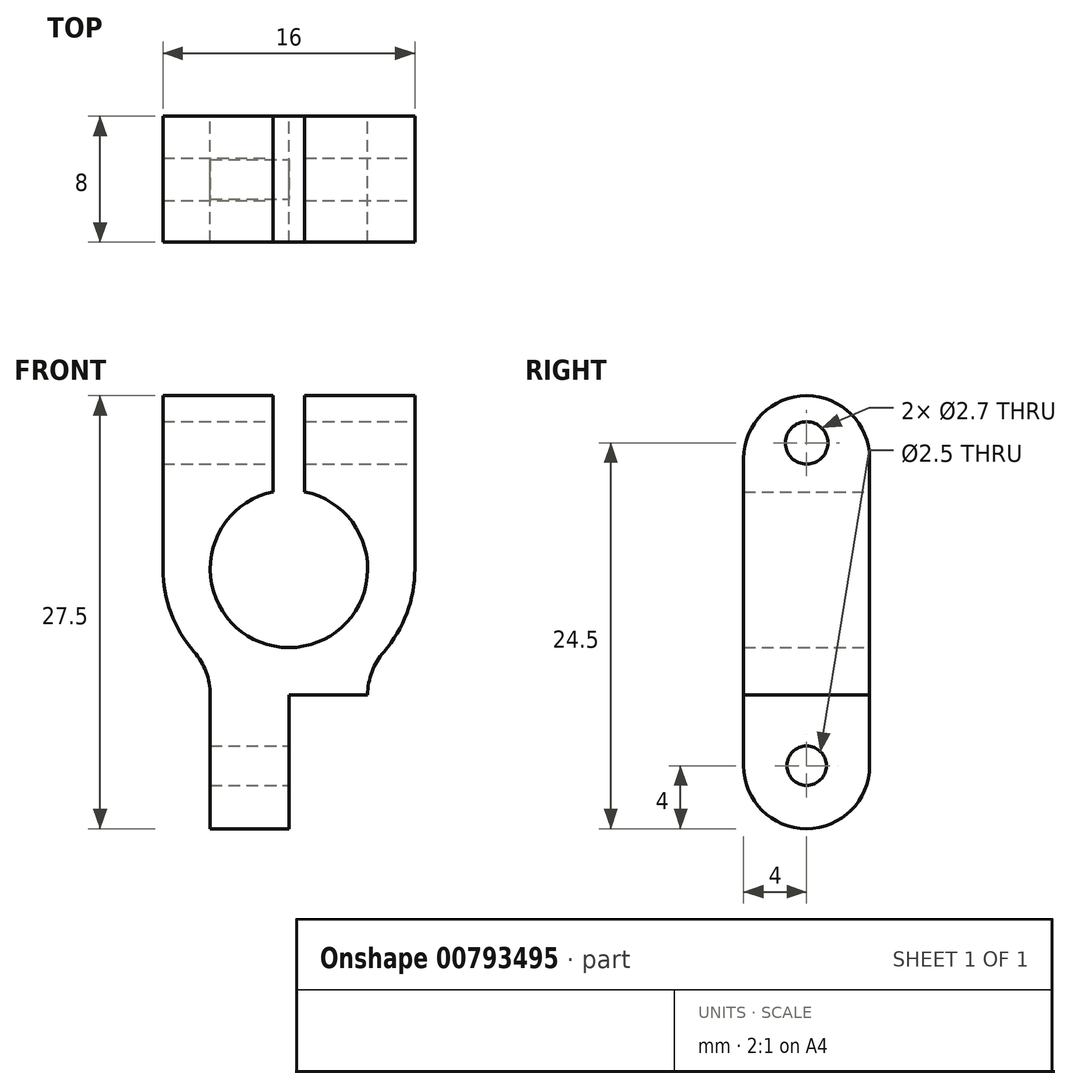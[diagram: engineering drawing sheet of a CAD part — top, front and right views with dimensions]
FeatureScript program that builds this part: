
annotation { "Feature Type Name" : "Feature", "Feature Type Description" : "" }
export const myFeature = defineFeature(function(context is Context, id is Id, definition is map)
    precondition{}
    {
        {
            var Q0;
            Q0=qCreatedBy(makeId("Front.planeOp"),FACE);
            var sketch = newSketch(context, id + "F0", { "sketchPlane" : qUnion([Q0])});
            skArc(sketch, "E0", {"start": v(-1, 4.9) * mm, "mid": v(0, -5) * mm, "end": v(1, 4.9) * mm});
            skLineSegment(sketch, "E1", {"start": v(-1, 11) * mm, "end": v(-1, 4.9) * mm});
            skLineSegment(sketch, "E2", {"start": v(1, 4.9) * mm, "end": v(1, 11) * mm});
            skLineSegment(sketch, "E3", {"start": v(-5, -8) * mm, "end": v(-5, -16.5) * mm});
            skLineSegment(sketch, "E4", {"start": v(-8, 11) * mm, "end": v(-8, 0) * mm});
            skLineSegment(sketch, "E5", {"start": v(8, 11) * mm, "end": v(8, 0) * mm});
            skLineSegment(sketch, "E6", {"start": v(8, 11) * mm, "end": v(1, 11) * mm});
            skLineSegment(sketch, "E7.trimOffspring", {"start": v(-1, 11) * mm, "end": v(-8, 11) * mm});
            skLineSegment(sketch, "E8", {"start": v(-5, -16.5) * mm, "end": v(0, -16.5) * mm});
            skLineSegment(sketch, "E9", {"start": v(0, -8) * mm, "end": v(-9.17, -8) * mm, "construction": true});
            skLineSegment(sketch, "E10", {"start": v(5, -8) * mm, "end": v(0, -8) * mm});
            skLineSegment(sketch, "E11", {"start": v(0, -8) * mm, "end": v(0, -16.5) * mm});
            skArc(sketch, "E12", {"start": v(-8, 0) * mm, "mid": v(-7.5, -2.8) * mm, "end": v(-6.03, -5.26) * mm});
            skArc(sketch, "E13", {"start": v(-5, -8) * mm, "mid": v(-5.27, -6.54) * mm, "end": v(-6.03, -5.26) * mm});
            skArc(sketch, "E14.MirrorCS", {"start": v(5, -8) * mm, "mid": v(5.27, -6.54) * mm, "end": v(6.03, -5.26) * mm});
            skArc(sketch, "E15.MirrorCS", {"start": v(8, 0) * mm, "mid": v(7.5, -2.8) * mm, "end": v(6.03, -5.26) * mm});
            skSolve(sketch);
        }
        {
            var Q0;
            Q0=makeQuery(id+"F0.imprint","IMPRINT",FACE,{"disambiguationData":[TD([[makeQuery(id+"F0.imprint","IMPRINT",EDGE,{"derivedFrom":sQuery(id+"F0.wireOp",EDGE,"E0")}),-1.0]])]});
            var Q1;
            {var subQ0=sQuery(id+"F0.wireOp",EDGE,"E3");Q1=makeQuery(id+"F0.imprint","IMPRINT",FACE,{"disambiguationData":[TD([[makeQuery(id+"F0.imprint","IMPRINT",EDGE,{"derivedFrom":subQ0}),1.0]])]});}
            extrude(context, id + "F1", {"entities" : qUnion([Q0, Q1]), "endBound" : BoundingType.SYMMETRIC, "depth" : 8 * mm, "offsetDistance" : 25 * mm});
        }
        {
            var Q0;
            Q0=makeQuery(id+"F1.opExtrude","SWEPT_FACE",FACE,{"disambiguationData":[OSD([sQuery(id+"F0.wireOp",EDGE,"E5")])]});
            var sketch = newSketch(context, id + "F2", { "sketchPlane" : qUnion([Q0])});
            skCircle(sketch, "E16", {"center": v(0, 8) * mm, "radius": 1.35 * mm});
            skSolve(sketch);
        }
        {
            var Q0;
            Q0=makeQuery(id+"F2.imprint","IMPRINT",FACE,{"disambiguationData":[TD([[makeQuery(id+"F2.imprint","IMPRINT",EDGE,{"derivedFrom":sQuery(id+"F2.wireOp",EDGE,"E16")}),1.0]])]});
            var Q1;
            {var subQ0=sQuery(id+"F2.wireOp",EDGE,"nRwaLtps-0aPM-k6Bh-PqO4-CJdIWXvHlXeP");Q1=makeQuery(id+"F2.imprint","IMPRINT",FACE,{"disambiguationData":[TD([[makeQuery(id+"F2.imprint","IMPRINT",EDGE,{"derivedFrom":subQ0}),1.0]])]});}
            var Q2;
            {var subQ0=sQuery(id+"F2.wireOp",EDGE,"26d730cf-6a02-49fb-9eb9-cb2f17dd4a160.MirrorCS");Q2=makeQuery(id+"F2.imprint","IMPRINT",FACE,{"disambiguationData":[TD([[makeQuery(id+"F2.imprint","IMPRINT",EDGE,{"derivedFrom":subQ0}),-1.0]])]});}
            extrude(context, id + "F3", {"entities" : qUnion([Q0, Q1, Q2]), "operationType" : NewBodyOperationType.REMOVE, "oppositeDirection" : true, "depth" : 25 * mm, "offsetDistance" : 25 * mm});
        }
        {
            var Q0;
            Q0=makeQuery(id+"F1.opExtrude","SWEPT_FACE",FACE,{"disambiguationData":[OSD([sQuery(id+"F0.wireOp",EDGE,"E11")])]});
            var sketch = newSketch(context, id + "F4", { "sketchPlane" : qUnion([Q0])});
            skCircle(sketch, "E17", {"center": v(0, -12.5) * mm, "radius": 1.25 * mm});
            skSolve(sketch);
        }
        {
            var Q0;
            Q0=makeQuery(id+"F4.imprint","IMPRINT",FACE,{"disambiguationData":[TD([[makeQuery(id+"F4.imprint","IMPRINT",EDGE,{"derivedFrom":sQuery(id+"F4.wireOp",EDGE,"E17")}),1.0]])]});
            var Q1;
            {var subQ0=sQuery(id+"F4.wireOp",EDGE,"dgfmRsRT-HZR4-KMtm-UVD4-OGYZ9sb2hiea");var subQ1=sQuery(id+"F0.wireOp",EDGE,"URoOaodK-mer2-KlBf-KcxF-PiR6j1BPeDQ6");var subQ2=makeQuery(id+"F1.opExtrude","CAP_EDGE",EDGE,{"disambiguationData":[OSD([subQ1])],"isStart":false});var subQ3=makeQuery(id+"F4.imprint","INTERSECT",VERTEX,{"derivedFrom":[subQ2,sQuery(id+"F4.wireOp",EDGE,"iwAXt04E-8AKp-sdOK-APD1-idUJ9iq6WJ0X"),subQ0]});Q1=makeQuery(id+"F4.imprint","IMPRINT",FACE,{"disambiguationData":[TD([[makeQuery(id+"F4.imprint","IMPRINT",EDGE,{"disambiguationData":[TD([[subQ3,-1.0]])],"derivedFrom":subQ0}),-1.0]])]});}
            var Q2;
            {var subQ0=sQuery(id+"F4.wireOp",EDGE,"dgfmRsRT-HZR4-KMtm-UVD4-OGYZ9sb2hiea");var subQ1=sQuery(id+"F0.wireOp",EDGE,"URoOaodK-mer2-KlBf-KcxF-PiR6j1BPeDQ6");var subQ2=makeQuery(id+"F1.opExtrude","CAP_EDGE",EDGE,{"disambiguationData":[OSD([subQ1])],"isStart":true});var subQ3=makeQuery(id+"F4.imprint","INTERSECT",VERTEX,{"derivedFrom":[subQ2,sQuery(id+"F4.wireOp",EDGE,"2524a595-133a-427d-9363-88fda697d8180.MirrorCS"),subQ0]});Q2=makeQuery(id+"F4.imprint","IMPRINT",FACE,{"disambiguationData":[TD([[makeQuery(id+"F4.imprint","IMPRINT",EDGE,{"disambiguationData":[TD([[subQ3,1.0]])],"derivedFrom":subQ0}),-1.0]])]});}
            extrude(context, id + "F5", {"entities" : qUnion([Q0, Q1, Q2]), "operationType" : NewBodyOperationType.REMOVE, "oppositeDirection" : true, "depth" : 25 * mm, "offsetDistance" : 25 * mm});
        }
        {
            var Q0;
            Q0=makeQuery(id+"F1.opExtrude","CAP_EDGE",EDGE,{"disambiguationData":[OSD([sQuery(id+"F0.wireOp",EDGE,"E7.trimOffspring")])],"isStart":false});
            var Q1;
            Q1=makeQuery(id+"F1.opExtrude","CAP_EDGE",EDGE,{"disambiguationData":[OSD([sQuery(id+"F0.wireOp",EDGE,"E7.trimOffspring")])],"isStart":true});
            var Q2;
            Q2=makeQuery(id+"F1.opExtrude","CAP_EDGE",EDGE,{"disambiguationData":[OSD([sQuery(id+"F0.wireOp",EDGE,"E6")])],"isStart":true});
            var Q3;
            Q3=makeQuery(id+"F1.opExtrude","CAP_EDGE",EDGE,{"disambiguationData":[OSD([sQuery(id+"F0.wireOp",EDGE,"E8")])],"isStart":false});
            var Q4;
            Q4=makeQuery(id+"F1.opExtrude","CAP_EDGE",EDGE,{"disambiguationData":[OSD([sQuery(id+"F0.wireOp",EDGE,"E8")])],"isStart":true});
            var Q5;
            Q5=makeQuery(id+"F1.opExtrude","CAP_EDGE",EDGE,{"disambiguationData":[OSD([sQuery(id+"F0.wireOp",EDGE,"E6")])],"isStart":false});
            fillet(context, id + "F6", {"entities" : qUnion([Q0, Q1, Q2, Q3, Q4, Q5]), "radius" : 4 * mm, "tangentPropagation" : true, "allowEdgeOverflow" : false});
        }
    });
